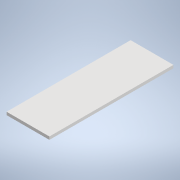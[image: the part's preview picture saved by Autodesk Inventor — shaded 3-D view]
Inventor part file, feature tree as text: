
AUTODESK INVENTOR PART (.ipt)
format: ipt  version: 2021.1 (Build 251245000, 245)  size: 92,160 bytes
history: native  units: in
note: dims shown in document units (in); Inventor stores cm internally (conversion verified against a paired STEP export)
features: other x5, reference x3, extrude x1, sketch x1
ambient origin geometry x8: Origin, YZ Plane, XZ Plane, XY Plane, X Axis, Y Axis, Z Axis, Center Point
bodies: Solid1 (feature_tree)
feature tree (10):
  extrude  "Extrusion1"  [1 undecoded]
  sketch  "Sketch1"  dims[d0=10.6299in d1=0.0in]
  reference  "Reference1"
  reference  "Reference2"
  reference  "Reference3"
  other  "<userpath>\Documents\Kerbal Kontroller\v.3.iam"
  other  "v.3.iam"
  other  "Sides:1"
  other  "Front:1"
  other  "Bottom:1"
note: 1 required parameter value undecoded (feature->parameter linkage not recoverable at this tier; creation-order binding heuristic only, values carry confidence <= 0.55)
